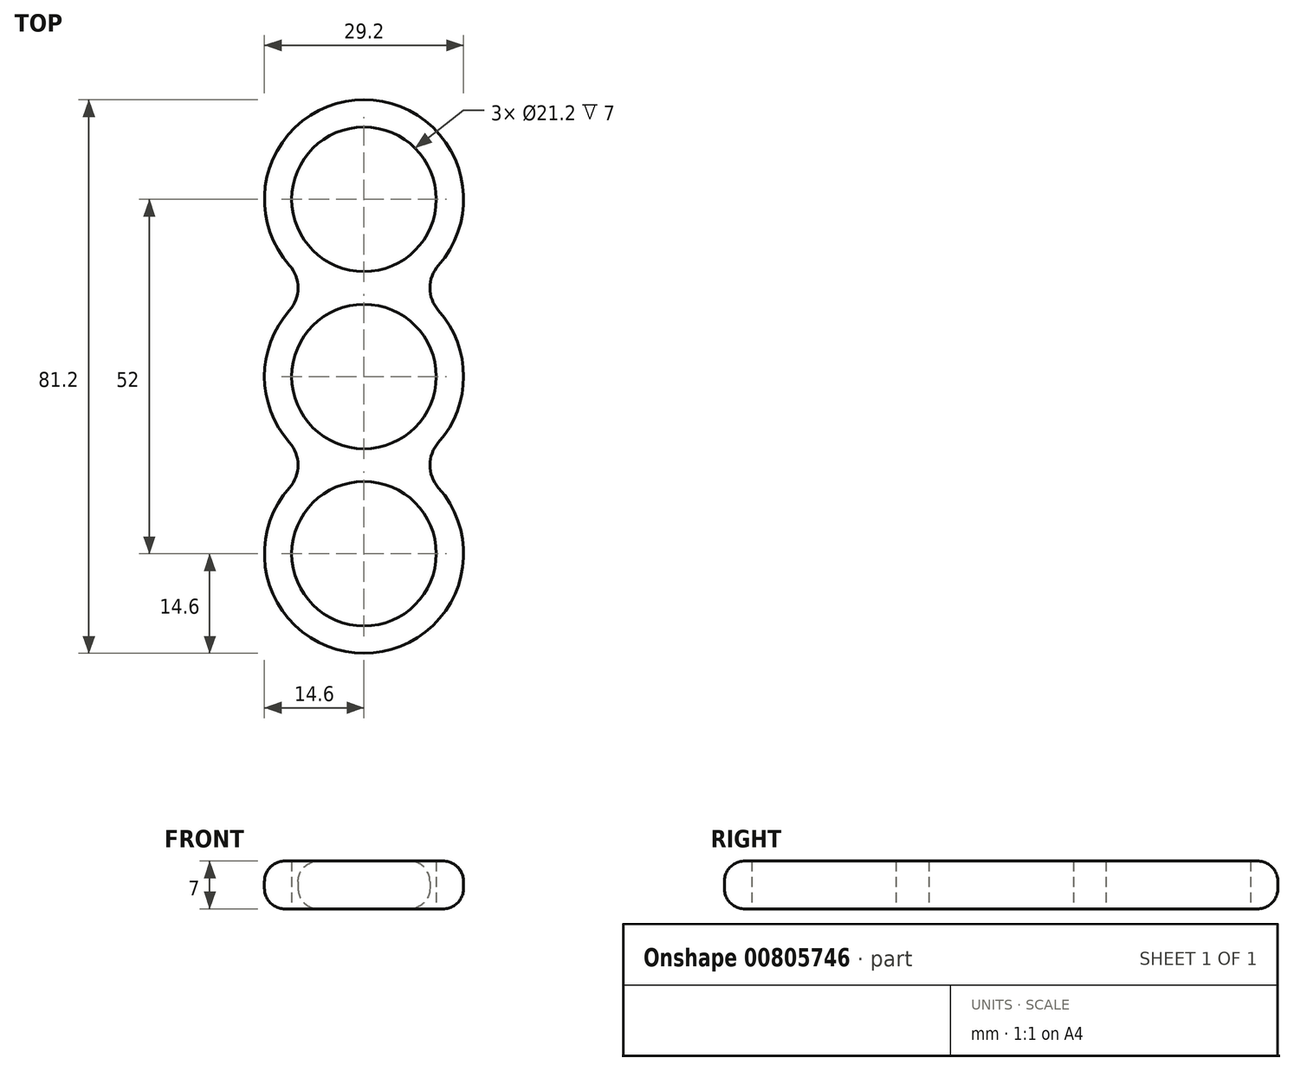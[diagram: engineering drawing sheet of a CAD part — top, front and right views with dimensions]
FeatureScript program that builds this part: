
annotation { "Feature Type Name" : "Feature", "Feature Type Description" : "" }
export const myFeature = defineFeature(function(context is Context, id is Id, definition is map)
    precondition{}
    {
        {
            var Q0;
            Q0=qCreatedBy(makeId("Top.planeOp"),FACE);
            var sketch = newSketch(context, id + "F0", { "sketchPlane" : qUnion([Q0])});
            skCircle(sketch, "E0", {"center": v(0, 0) * mm, "radius": 10.6 * mm});
            skCircle(sketch, "E1", {"center": v(0, 26) * mm, "radius": 10.6 * mm});
            skCircle(sketch, "E2", {"center": v(0, -26) * mm, "radius": 10.6 * mm});
            skCircle(sketch, "E3.0", {"center": v(0, 26) * mm, "radius": 14.6 * mm, "construction": true});
            skCircle(sketch, "E4.0", {"center": v(0, 0) * mm, "radius": 14.6 * mm, "construction": true});
            skCircle(sketch, "E5.0", {"center": v(0, -26) * mm, "radius": 14.6 * mm, "construction": true});
            skArc(sketch, "E6", {"start": v(-10.93, 16.32) * mm, "mid": v(0, 40.6) * mm, "end": v(10.93, 16.32) * mm});
            skArc(sketch, "E7", {"start": v(-10.93, 9.68) * mm, "mid": v(-14.6, 0) * mm, "end": v(-10.93, -9.68) * mm});
            skArc(sketch, "E8", {"start": v(-10.93, -16.32) * mm, "mid": v(0, -40.6) * mm, "end": v(10.93, -16.32) * mm});
            skArc(sketch, "E9", {"start": v(10.93, -9.68) * mm, "mid": v(14.6, 0) * mm, "end": v(10.93, 9.68) * mm});
            skPoint(sketch, "E10.visualSharp", {"position": v(-6.65, 13) * mm});
            skArc(sketch, "E10.filletArc", {"start": v(-10.93, 9.68) * mm, "mid": v(-9.67, 13) * mm, "end": v(-10.93, 16.32) * mm});
            skPoint(sketch, "E11.visualSharp", {"position": v(6.65, 13) * mm});
            skArc(sketch, "E11.filletArc", {"start": v(10.93, 16.32) * mm, "mid": v(9.67, 13) * mm, "end": v(10.93, 9.68) * mm});
            skPoint(sketch, "E12.visualSharp", {"position": v(6.65, -13) * mm});
            skArc(sketch, "E12.filletArc", {"start": v(10.93, -9.68) * mm, "mid": v(9.67, -13) * mm, "end": v(10.93, -16.32) * mm});
            skPoint(sketch, "E13.visualSharp", {"position": v(-6.65, -13) * mm});
            skArc(sketch, "E13.filletArc", {"start": v(-10.93, -16.32) * mm, "mid": v(-9.67, -13) * mm, "end": v(-10.93, -9.68) * mm});
            skSolve(sketch);
        }
        {
            var Q0;
            Q0 = qSketchRegion(id + "F0", true);
            extrude(context, id + "F1", {"entities" : qUnion([Q0]), "depth" : 7 * mm, "offsetDistance" : 25 * mm});
        }
        {
            var Q0;
            Q0=makeQuery(id+"F1.opExtrude","CAP_EDGE",EDGE,{"disambiguationData":[OSD([sQuery(id+"F0.wireOp",EDGE,"E6")])],"isStart":false});
            var Q1;
            Q1=makeQuery(id+"F1.opExtrude","CAP_EDGE",EDGE,{"disambiguationData":[OSD([sQuery(id+"F0.wireOp",EDGE,"E6")])],"isStart":true});
            fillet(context, id + "F2", {"entities" : qUnion([Q0, Q1]), "radius" : 3 * mm, "tangentPropagation" : true, "allowEdgeOverflow" : false});
        }
    });
